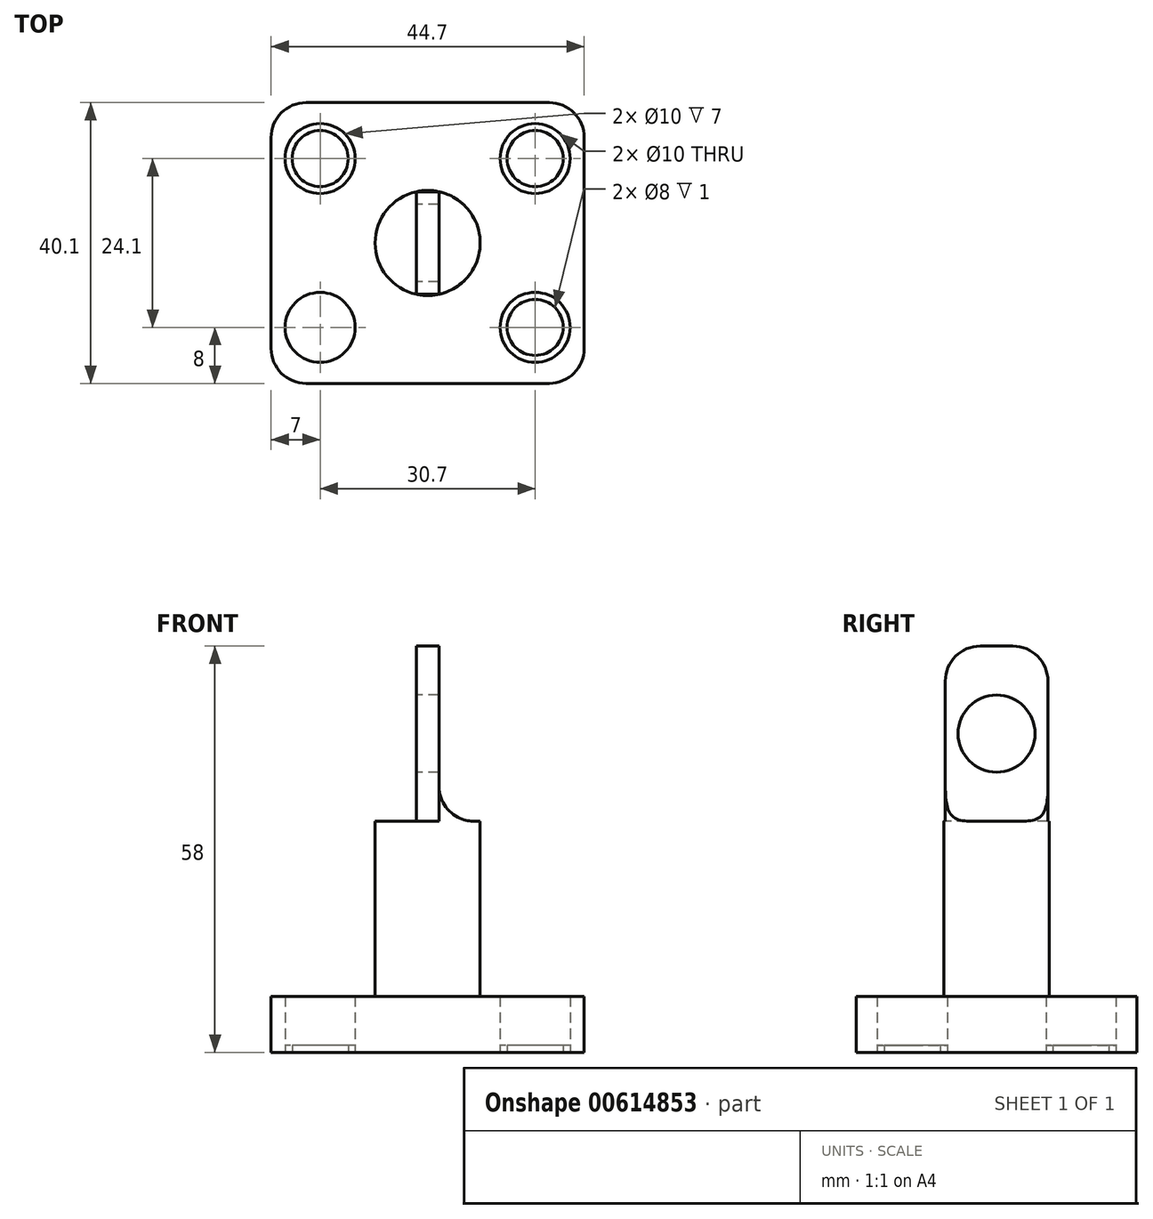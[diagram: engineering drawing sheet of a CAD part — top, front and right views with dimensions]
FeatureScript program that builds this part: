
annotation { "Feature Type Name" : "Feature", "Feature Type Description" : "" }
export const myFeature = defineFeature(function(context is Context, id is Id, definition is map)
    precondition{}
    {
        {
            var Q0;
            Q0=qCreatedBy(makeId("Top.planeOp"),FACE);
            var sketch = newSketch(context, id + "F0", { "sketchPlane" : qUnion([Q0])});
            skLineSegment(sketch, "E0.rect.bottom", {"start": v(-22.35, 20.05) * mm, "end": v(22.35, 20.05) * mm});
            skLineSegment(sketch, "E0.rect.top", {"start": v(-22.35, -20.05) * mm, "end": v(22.35, -20.05) * mm});
            skLineSegment(sketch, "E0.rect.left", {"start": v(-22.35, 20.05) * mm, "end": v(-22.35, -20.05) * mm});
            skLineSegment(sketch, "E0.rect.right", {"start": v(22.35, 20.05) * mm, "end": v(22.35, -20.05) * mm});
            skPoint(sketch, "E0.rect.middle", {"position": v(0, 0) * mm});
            skLineSegment(sketch, "E1", {"start": v(0, 20.05) * mm, "end": v(0, -20.05) * mm, "construction": true});
            skLineSegment(sketch, "E2", {"start": v(-22.35, 0) * mm, "end": v(22.35, 0) * mm, "construction": true});
            skCircle(sketch, "E3", {"center": v(-15.35, 12.05) * mm, "radius": 4 * mm});
            skCircle(sketch, "E4", {"center": v(-15.35, 12.05) * mm, "radius": 5 * mm});
            skCircle(sketch, "E5.MirrorC", {"center": v(15.35, 12.05) * mm, "radius": 4 * mm});
            skCircle(sketch, "E6.MirrorC", {"center": v(15.35, 12.05) * mm, "radius": 5 * mm});
            skLineSegment(sketch, "E7.MirrorCS", {"start": v(0, -20.05) * mm, "end": v(0, 20.05) * mm, "construction": true});
            skCircle(sketch, "E8.MirrorC", {"center": v(-15.35, -12.05) * mm, "radius": 5 * mm});
            skCircle(sketch, "E9.MirrorC", {"center": v(-15.35, -12.05) * mm, "radius": 4 * mm});
            skCircle(sketch, "E10.MirrorC", {"center": v(15.35, -12.05) * mm, "radius": 5 * mm});
            skCircle(sketch, "E11.MirrorC", {"center": v(15.35, -12.05) * mm, "radius": 4 * mm});
            skSolve(sketch);
        }
        {
            var Q0;
            Q0=makeQuery(id+"F0.imprint","IMPRINT",FACE,{"disambiguationData":[TD([[makeQuery(id+"F0.imprint","IMPRINT",EDGE,{"derivedFrom":sQuery(id+"F0.wireOp",EDGE,"E0.rect.bottom")}),-1.0]])]});
            extrude(context, id + "F1", {"entities" : qUnion([Q0]), "depth" : 8 * mm});
        }
        {
            var Q0;
            Q0=makeQuery(id+"F0.imprint","IMPRINT",FACE,{"disambiguationData":[TD([[makeQuery(id+"F0.imprint","IMPRINT",EDGE,{"derivedFrom":sQuery(id+"F0.wireOp",EDGE,"E5.MirrorC")}),1.0]])]});
            var Q1;
            Q1=makeQuery(id+"F0.imprint","IMPRINT",FACE,{"disambiguationData":[TD([[makeQuery(id+"F0.imprint","IMPRINT",EDGE,{"derivedFrom":sQuery(id+"F0.wireOp",EDGE,"E10.MirrorC")}),1.0]])]});
            var Q2;
            Q2=makeQuery(id+"F0.imprint","IMPRINT",FACE,{"disambiguationData":[TD([[makeQuery(id+"F0.imprint","IMPRINT",EDGE,{"derivedFrom":sQuery(id+"F0.wireOp",EDGE,"E8.MirrorC")}),-1.0]])]});
            var Q3;
            Q3=makeQuery(id+"F0.imprint","IMPRINT",FACE,{"disambiguationData":[TD([[makeQuery(id+"F0.imprint","IMPRINT",EDGE,{"derivedFrom":sQuery(id+"F0.wireOp",EDGE,"E3")}),-1.0]])]});
            extrude(context, id + "F2", {"entities" : qUnion([Q0, Q1, Q2, Q3]), "operationType" : NewBodyOperationType.ADD, "depth" : 1 * mm});
        }
        {
            var Q0;
            Q0=makeQuery(id+"F1.opExtrude","CAP_FACE",FACE,{"disambiguationData":[OSD([sQuery(id+"F0.wireOp",EDGE,"E0.rect.bottom"),sQuery(id+"F0.wireOp",EDGE,"E0.rect.top"),sQuery(id+"F0.wireOp",EDGE,"E0.rect.left"),sQuery(id+"F0.wireOp",EDGE,"E0.rect.right"),sQuery(id+"F0.wireOp",EDGE,"E4"),sQuery(id+"F0.wireOp",EDGE,"E6.MirrorC"),sQuery(id+"F0.wireOp",EDGE,"E8.MirrorC"),sQuery(id+"F0.wireOp",EDGE,"E10.MirrorC")])],"isStart":false});
            var sketch = newSketch(context, id + "F3", { "sketchPlane" : qUnion([Q0])});
            skCircle(sketch, "E12", {"center": v(0, 0) * mm, "radius": 7.5 * mm});
            skSolve(sketch);
        }
        {
            var Q0;
            Q0 = qSketchRegion(id + "F3", true);
            extrude(context, id + "F4", {"entities" : qUnion([Q0]), "operationType" : NewBodyOperationType.ADD, "depth" : 25 * mm, "offsetDistance" : 25 * mm});
        }
        {
            var Q0;
            Q0=makeQuery(id+"F4.opExtrude","CAP_FACE",FACE,{"disambiguationData":[OSD([sQuery(id+"F3.wireOp",EDGE,"E12")])],"isStart":false});
            var sketch = newSketch(context, id + "F5", { "sketchPlane" : qUnion([Q0])});
            skLineSegment(sketch, "E13.bottom", {"start": v(-1.61, 7.33) * mm, "end": v(1.61, 7.33) * mm});
            skLineSegment(sketch, "E13.top", {"start": v(-1.61, -7.33) * mm, "end": v(1.61, -7.33) * mm});
            skLineSegment(sketch, "E13.left", {"start": v(-1.61, 7.33) * mm, "end": v(-1.61, -7.33) * mm});
            skLineSegment(sketch, "E13.right", {"start": v(1.61, 7.33) * mm, "end": v(1.61, -7.33) * mm});
            skPoint(sketch, "E13.middle", {"position": v(0, 0) * mm});
            skSolve(sketch);
        }
        {
            var Q0;
            Q0 = qSketchRegion(id + "F5", true);
            extrude(context, id + "F6", {"entities" : qUnion([Q0]), "operationType" : NewBodyOperationType.ADD, "depth" : 25 * mm, "offsetDistance" : 25 * mm});
        }
        {
            var Q0;
            Q0=makeQuery(id+"F6.opExtrude","SWEPT_FACE",FACE,{"disambiguationData":[OSD([sQuery(id+"F5.wireOp",EDGE,"E13.left")])]});
            var sketch = newSketch(context, id + "F7", { "sketchPlane" : qUnion([Q0])});
            skPoint(sketch, "E14", {"position": v(0, 45.5) * mm});
            skPoint(sketch, "E14.positionSnap0", {"position": v(-7.33, 45.5) * mm});
            skPoint(sketch, "E14.positionSnap1", {"position": v(0, 58) * mm});
            skCircle(sketch, "E15", {"center": v(0, 45.5) * mm, "radius": 5.5 * mm});
            skPoint(sketch, "E16.0.1.end.orphan", {"position": v(7.33, 58) * mm});
            skPoint(sketch, "E16.0.2.end.orphan", {"position": v(-7.33, 58) * mm});
            skPoint(sketch, "E16.0.0.end.orphan", {"position": v(7.33, 33) * mm});
            skPoint(sketch, "E16.0.0.start.orphan", {"position": v(-7.33, 33) * mm});
            skSolve(sketch);
        }
        {
            var Q0;
            Q0 = qSketchRegion(id + "F7", true);
            extrude(context, id + "F8", {"entities" : qUnion([Q0]), "operationType" : NewBodyOperationType.REMOVE, "oppositeDirection" : true, "depth" : 10 * mm, "offsetDistance" : 25 * mm});
        }
        {
            var Q0;
            Q0=makeQuery(id+"F6.opExtrude","CAP_EDGE",EDGE,{"disambiguationData":[OSD([sQuery(id+"F5.wireOp",EDGE,"E13.bottom")])],"isStart":false});
            var Q1;
            Q1=makeQuery(id+"F6.opExtrude","CAP_EDGE",EDGE,{"disambiguationData":[OSD([sQuery(id+"F5.wireOp",EDGE,"E13.top")])],"isStart":false});
            var Q2;
            Q2=makeQuery(id+"F1.opExtrude","SWEPT_EDGE",EDGE,{"disambiguationData":[OSD([sQuery(id+"F0.wireOp",EDGE,"E0.rect.bottom"),sQuery(id+"F0.wireOp",EDGE,"E0.rect.left")])]});
            var Q3;
            Q3=makeQuery(id+"F1.opExtrude","SWEPT_EDGE",EDGE,{"disambiguationData":[OSD([sQuery(id+"F0.wireOp",EDGE,"E0.rect.top"),sQuery(id+"F0.wireOp",EDGE,"E0.rect.left")])]});
            var Q4;
            Q4=makeQuery(id+"F1.opExtrude","SWEPT_EDGE",EDGE,{"disambiguationData":[OSD([sQuery(id+"F0.wireOp",EDGE,"E0.rect.top"),sQuery(id+"F0.wireOp",EDGE,"E0.rect.right")])]});
            var Q5;
            Q5=makeQuery(id+"F1.opExtrude","SWEPT_EDGE",EDGE,{"disambiguationData":[OSD([sQuery(id+"F0.wireOp",EDGE,"E0.rect.bottom"),sQuery(id+"F0.wireOp",EDGE,"E0.rect.right")])]});
            fillet(context, id + "F9", {"entities" : qUnion([Q0, Q1, Q2, Q3, Q4, Q5]), "radius" : 5 * mm, "tangentPropagation" : true, "allowEdgeOverflow" : false});
        }
        {
            var Q0;
            Q0=makeQuery(id+"F6.opExtrude","CAP_EDGE",EDGE,{"disambiguationData":[OSD([sQuery(id+"F5.wireOp",EDGE,"E13.right")])],"isStart":true});
            var Q1;
            Q1=makeQuery(id+"F6.opExtrude","CAP_EDGE",EDGE,{"disambiguationData":[OSD([sQuery(id+"F5.wireOp",EDGE,"E13.left")])],"isStart":true});
            var Q2;
            Q2=makeQuery(id+"F4.opExtrude","CAP_EDGE",EDGE,{"disambiguationData":[OSD([sQuery(id+"F3.wireOp",EDGE,"E12")])],"isStart":true});
            fillet(context, id + "F10", {"entities" : qUnion([Q0, Q1, Q2]), "radius" : 5 * mm, "tangentPropagation" : true, "allowEdgeOverflow" : false});
        }
    });
